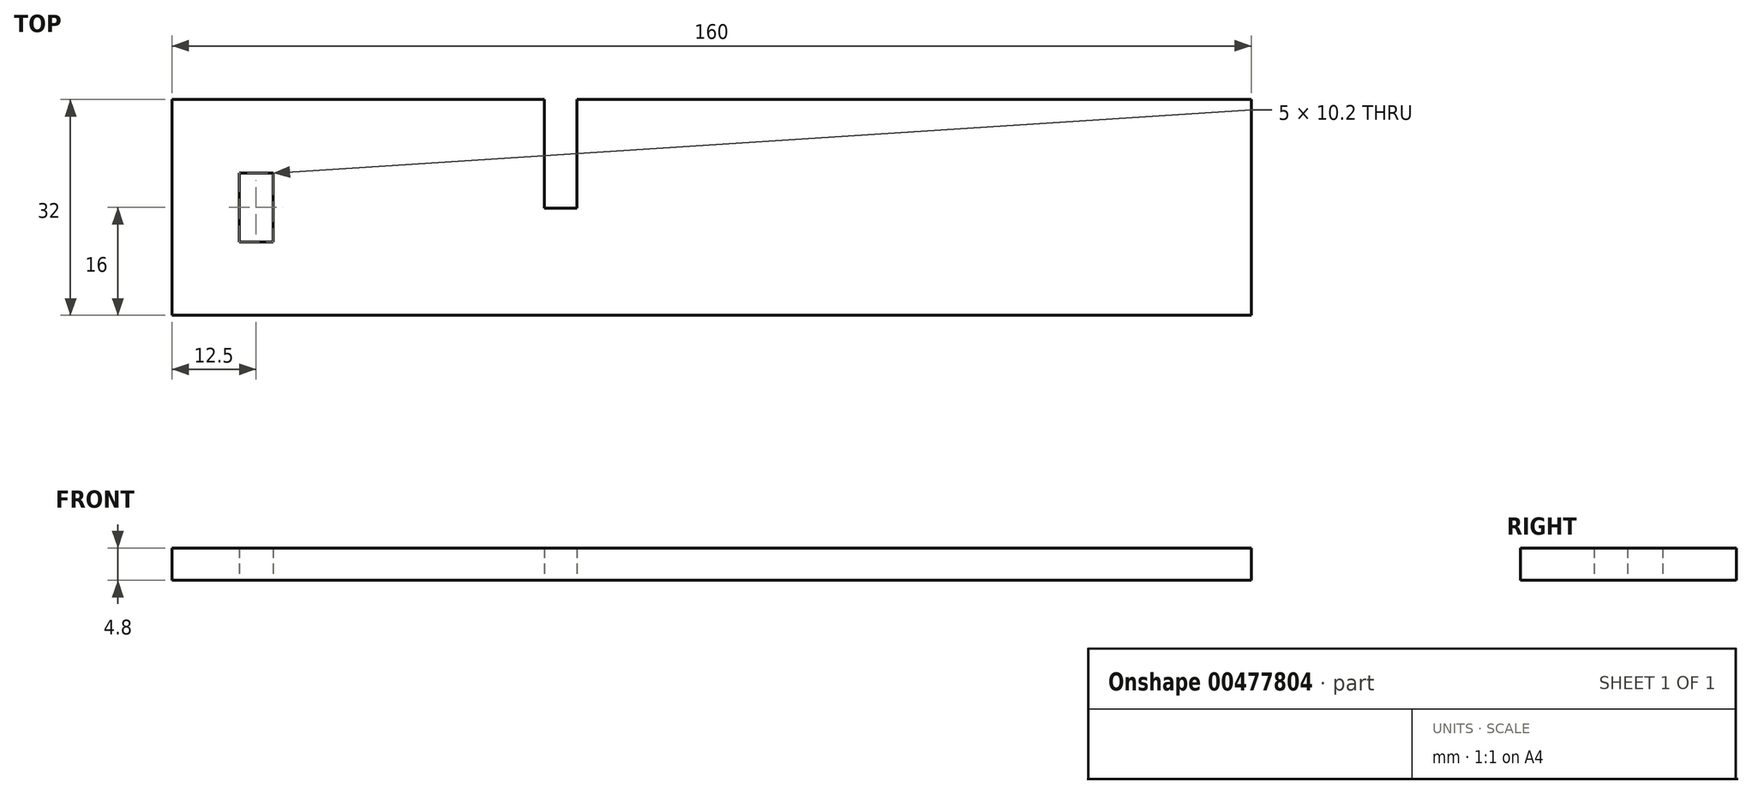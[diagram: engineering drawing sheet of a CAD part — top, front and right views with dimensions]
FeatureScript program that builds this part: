
annotation { "Feature Type Name" : "Feature", "Feature Type Description" : "" }
export const myFeature = defineFeature(function(context is Context, id is Id, definition is map)
    precondition{}
    {
        {
            var Q0;
            Q0=qCreatedBy(makeId("Top.planeOp"),FACE);
            var sketch = newSketch(context, id + "F0", { "sketchPlane" : qUnion([Q0])});
            skLineSegment(sketch, "E0.bottom", {"start": v(0, 0) * mm, "end": v(160, 0) * mm});
            skLineSegment(sketch, "E0.top", {"start": v(0, 32) * mm, "end": v(160, 32) * mm});
            skLineSegment(sketch, "E0.left", {"start": v(0, 0) * mm, "end": v(0, 32) * mm});
            skLineSegment(sketch, "E0.right", {"start": v(160, 0) * mm, "end": v(160, 32) * mm});
            skLineSegment(sketch, "E1.bottom", {"start": v(55.2, 32) * mm, "end": v(60, 32) * mm});
            skLineSegment(sketch, "E1.top", {"start": v(55.2, 15.9) * mm, "end": v(60, 15.9) * mm});
            skLineSegment(sketch, "E1.left", {"start": v(55.2, 32) * mm, "end": v(55.2, 15.9) * mm});
            skLineSegment(sketch, "E1.right", {"start": v(60, 32) * mm, "end": v(60, 15.9) * mm});
            skLineSegment(sketch, "E2.bottom", {"start": v(10, 21.1) * mm, "end": v(15, 21.1) * mm});
            skLineSegment(sketch, "E2.top", {"start": v(10, 10.9) * mm, "end": v(15, 10.9) * mm});
            skLineSegment(sketch, "E2.left", {"start": v(10, 21.1) * mm, "end": v(10, 10.9) * mm});
            skLineSegment(sketch, "E2.right", {"start": v(15, 21.1) * mm, "end": v(15, 10.9) * mm});
            skSolve(sketch);
        }
        {
            var Q0;
            Q0=makeQuery(id+"F0.imprint","IMPRINT",FACE,{"disambiguationData":[TD([[makeQuery(id+"F0.imprint","IMPRINT",EDGE,{"derivedFrom":sQuery(id+"F0.wireOp",EDGE,"E0.bottom")}),1.0]])]});
            extrude(context, id + "F1", {"entities" : qUnion([Q0]), "depth" : 4.8 * mm});
        }
    });
